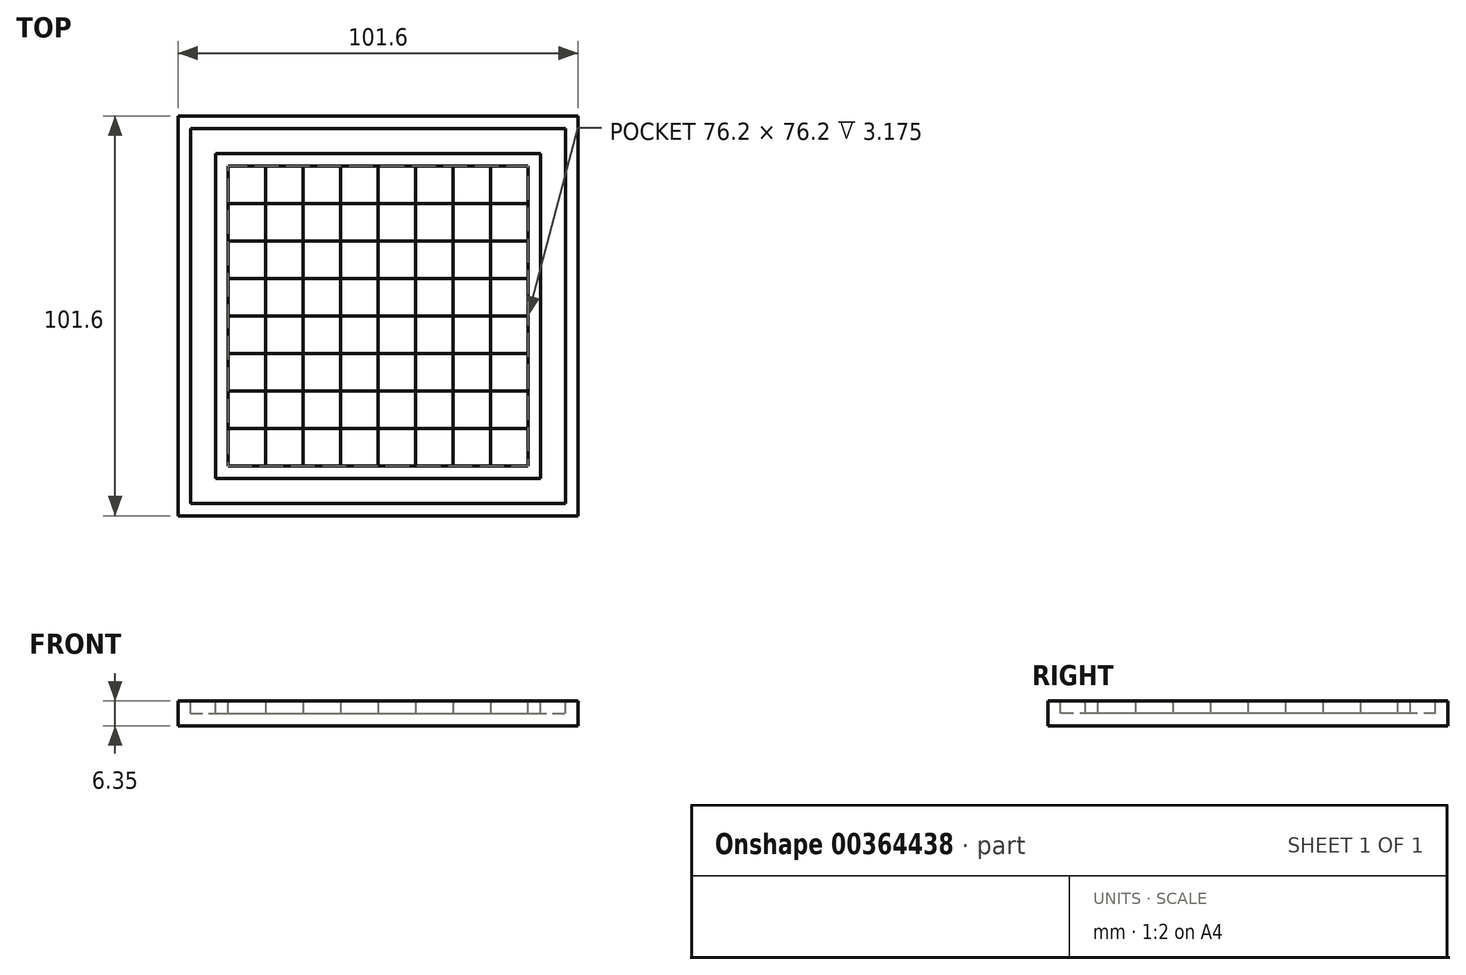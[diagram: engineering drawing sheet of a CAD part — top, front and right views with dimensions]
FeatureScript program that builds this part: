
annotation { "Feature Type Name" : "Feature", "Feature Type Description" : "" }
export const myFeature = defineFeature(function(context is Context, id is Id, definition is map)
    precondition{}
    {
        {
            var Q0;
            Q0=qCreatedBy(makeId("Top.planeOp"),FACE);
            var sketch = newSketch(context, id + "F0", { "sketchPlane" : qUnion([Q0])});
            skLineSegment(sketch, "E0.bottom", {"start": v(-50.8, 50.8) * mm, "end": v(50.8, 50.8) * mm});
            skLineSegment(sketch, "E0.top", {"start": v(-50.8, -50.8) * mm, "end": v(50.8, -50.8) * mm});
            skLineSegment(sketch, "E0.left", {"start": v(-50.8, 50.8) * mm, "end": v(-50.8, -50.8) * mm});
            skLineSegment(sketch, "E0.right", {"start": v(50.8, 50.8) * mm, "end": v(50.8, -50.8) * mm});
            skPoint(sketch, "E0.middle", {"position": v(0, 0) * mm});
            skSolve(sketch);
        }
        {
            var Q0;
            Q0 = qSketchRegion(id + "F0", true);
            extrude(context, id + "F1", {"entities" : qUnion([Q0]), "depth" : 6.35 * mm});
        }
        {
            var Q0;
            Q0=makeQuery(id+"F1.opExtrude","CAP_FACE",FACE,{"disambiguationData":[OSD([sQuery(id+"F0.wireOp",EDGE,"E0.bottom"),sQuery(id+"F0.wireOp",EDGE,"E0.top"),sQuery(id+"F0.wireOp",EDGE,"E0.left"),sQuery(id+"F0.wireOp",EDGE,"E0.right")])],"isStart":false});
            var sketch = newSketch(context, id + "F2", { "sketchPlane" : qUnion([Q0])});
            skLineSegment(sketch, "E1.bottom", {"start": v(-47.63, 47.63) * mm, "end": v(47.63, 47.63) * mm});
            skLineSegment(sketch, "E1.top", {"start": v(-47.63, -47.63) * mm, "end": v(47.63, -47.63) * mm});
            skLineSegment(sketch, "E1.left", {"start": v(-47.63, 47.63) * mm, "end": v(-47.63, -47.63) * mm});
            skLineSegment(sketch, "E1.right", {"start": v(47.63, 47.63) * mm, "end": v(47.63, -47.63) * mm});
            skPoint(sketch, "E1.middle", {"position": v(0, 0) * mm});
            skLineSegment(sketch, "E2.bottom", {"start": v(-41.28, 41.28) * mm, "end": v(41.28, 41.28) * mm});
            skLineSegment(sketch, "E2.top", {"start": v(-41.28, -41.27) * mm, "end": v(41.28, -41.27) * mm});
            skLineSegment(sketch, "E2.left", {"start": v(-41.28, 41.28) * mm, "end": v(-41.28, -41.28) * mm});
            skLineSegment(sketch, "E2.right", {"start": v(41.28, 41.28) * mm, "end": v(41.28, -41.28) * mm});
            skLineSegment(sketch, "E3.bottom", {"start": v(-38.1, 38.1) * mm, "end": v(38.1, 38.1) * mm});
            skLineSegment(sketch, "E3.top", {"start": v(-38.1, -38.1) * mm, "end": v(38.1, -38.1) * mm});
            skLineSegment(sketch, "E3.left", {"start": v(-38.1, 38.1) * mm, "end": v(-38.1, -38.1) * mm});
            skLineSegment(sketch, "E3.right", {"start": v(38.1, 38.1) * mm, "end": v(38.1, -38.1) * mm});
            skSolve(sketch);
        }
        {
            var Q0;
            Q0=makeQuery(id+"F2.imprint","IMPRINT",FACE,{"disambiguationData":[TD([[makeQuery(id+"F2.imprint","IMPRINT",EDGE,{"derivedFrom":sQuery(id+"F2.wireOp",EDGE,"E1.bottom")}),-1.0]])]});
            extrude(context, id + "F3", {"entities" : qUnion([Q0]), "operationType" : NewBodyOperationType.REMOVE, "oppositeDirection" : true, "depth" : 3.17 * mm});
        }
        {
            var Q0;
            Q0=makeQuery(id+"F2.imprint","IMPRINT",FACE,{"disambiguationData":[TD([[makeQuery(id+"F2.imprint","IMPRINT",EDGE,{"derivedFrom":sQuery(id+"F2.wireOp",EDGE,"E3.bottom")}),-1.0]])]});
            extrude(context, id + "F4", {"entities" : qUnion([Q0]), "operationType" : NewBodyOperationType.REMOVE, "oppositeDirection" : true, "depth" : 3.17 * mm});
        }
        {
            var Q0;
            Q0=makeQuery(id+"F4.boolean.opBoolean","COPY",FACE,{"derivedFrom":makeQuery(id+"F4.opExtrude","CAP_FACE",FACE,{"disambiguationData":[OSD([sQuery(id+"F2.wireOp",EDGE,"E3.bottom"),sQuery(id+"F2.wireOp",EDGE,"E3.top"),sQuery(id+"F2.wireOp",EDGE,"E3.left"),sQuery(id+"F2.wireOp",EDGE,"E3.right")])],"isStart":false})});
            var sketch = newSketch(context, id + "F5", { "sketchPlane" : qUnion([Q0])});
            skLineSegment(sketch, "E4", {"start": v(-28.58, 38.1) * mm, "end": v(-28.58, -38.1) * mm});
            skLineSegment(sketch, "E5", {"start": v(-19.05, 38.1) * mm, "end": v(-19.05, -38.1) * mm});
            skLineSegment(sketch, "E6", {"start": v(-9.53, 38.1) * mm, "end": v(-9.52, -38.1) * mm});
            skLineSegment(sketch, "E7", {"start": v(0, 38.1) * mm, "end": v(0, -38.1) * mm});
            skLineSegment(sketch, "E8", {"start": v(9.52, 38.1) * mm, "end": v(9.53, -38.1) * mm});
            skLineSegment(sketch, "E9", {"start": v(19.05, 38.1) * mm, "end": v(19.05, -38.1) * mm});
            skLineSegment(sketch, "E10", {"start": v(28.57, 38.1) * mm, "end": v(28.57, -38.1) * mm});
            skLineSegment(sketch, "E11", {"start": v(-38.1, 28.58) * mm, "end": v(38.1, 28.58) * mm});
            skLineSegment(sketch, "E12", {"start": v(-38.1, 19.05) * mm, "end": v(38.1, 19.05) * mm});
            skLineSegment(sketch, "E13", {"start": v(-38.1, 9.53) * mm, "end": v(38.1, 9.53) * mm});
            skLineSegment(sketch, "E14", {"start": v(-38.1, 0) * mm, "end": v(38.1, 0) * mm});
            skLineSegment(sketch, "E15", {"start": v(-38.1, -9.53) * mm, "end": v(38.1, -9.53) * mm});
            skLineSegment(sketch, "E16", {"start": v(-38.1, -19.05) * mm, "end": v(38.1, -19.05) * mm});
            skLineSegment(sketch, "E17", {"start": v(-38.1, -28.58) * mm, "end": v(38.1, -28.58) * mm});
            skSolve(sketch);
        }
        {
            var Q0;
            {var subQ0=sQuery(id+"F5.wireOp",EDGE,"E9");var subQ1=makeQuery(id+"F4.boolean.opBoolean","COPY",EDGE,{"derivedFrom":makeQuery(id+"F4.opExtrude","CAP_EDGE",EDGE,{"disambiguationData":[OSD([sQuery(id+"F2.wireOp",EDGE,"E3.top")])],"isStart":false})});var subQ2=makeQuery(id+"F5.imprint","INTERSECT",VERTEX,{"derivedFrom":[subQ1,subQ0]});Q0=makeQuery(id+"F5.imprint","IMPRINT",FACE,{"disambiguationData":[TD([[makeQuery(id+"F5.imprint","IMPRINT",EDGE,{"disambiguationData":[TD([[subQ2,1.0]])],"derivedFrom":subQ0}),1.0]])]});}
            var Q1;
            {var subQ0=sQuery(id+"F5.wireOp",EDGE,"E7");var subQ1=makeQuery(id+"F4.boolean.opBoolean","COPY",EDGE,{"derivedFrom":makeQuery(id+"F4.opExtrude","CAP_EDGE",EDGE,{"disambiguationData":[OSD([sQuery(id+"F2.wireOp",EDGE,"E3.top")])],"isStart":false})});var subQ2=makeQuery(id+"F5.imprint","INTERSECT",VERTEX,{"derivedFrom":[subQ1,subQ0]});Q1=makeQuery(id+"F5.imprint","IMPRINT",FACE,{"disambiguationData":[TD([[makeQuery(id+"F5.imprint","IMPRINT",EDGE,{"disambiguationData":[TD([[subQ2,1.0]])],"derivedFrom":subQ0}),1.0]])]});}
            var Q2;
            {var subQ0=sQuery(id+"F5.wireOp",EDGE,"E5");var subQ1=makeQuery(id+"F4.boolean.opBoolean","COPY",EDGE,{"derivedFrom":makeQuery(id+"F4.opExtrude","CAP_EDGE",EDGE,{"disambiguationData":[OSD([sQuery(id+"F2.wireOp",EDGE,"E3.top")])],"isStart":false})});var subQ2=makeQuery(id+"F5.imprint","INTERSECT",VERTEX,{"derivedFrom":[subQ1,subQ0]});Q2=makeQuery(id+"F5.imprint","IMPRINT",FACE,{"disambiguationData":[TD([[makeQuery(id+"F5.imprint","IMPRINT",EDGE,{"disambiguationData":[TD([[subQ2,1.0]])],"derivedFrom":subQ0}),1.0]])]});}
            var Q3;
            {var subQ0=sQuery(id+"F5.wireOp",EDGE,"E4");var subQ1=makeQuery(id+"F4.boolean.opBoolean","COPY",EDGE,{"derivedFrom":makeQuery(id+"F4.opExtrude","CAP_EDGE",EDGE,{"disambiguationData":[OSD([sQuery(id+"F2.wireOp",EDGE,"E3.top")])],"isStart":false})});var subQ2=makeQuery(id+"F5.imprint","INTERSECT",VERTEX,{"derivedFrom":[subQ1,subQ0]});Q3=makeQuery(id+"F5.imprint","IMPRINT",FACE,{"disambiguationData":[TD([[makeQuery(id+"F5.imprint","IMPRINT",EDGE,{"disambiguationData":[TD([[subQ2,1.0]])],"derivedFrom":subQ0}),-1.0]])]});}
            var Q4;
            {var subQ0=sQuery(id+"F5.wireOp",EDGE,"E16");var subQ1=sQuery(id+"F5.wireOp",EDGE,"E4");var subQ2=makeQuery(id+"F5.imprint","INTERSECT",VERTEX,{"derivedFrom":[subQ1,subQ0]});Q4=makeQuery(id+"F5.imprint","IMPRINT",FACE,{"disambiguationData":[TD([[makeQuery(id+"F5.imprint","IMPRINT",EDGE,{"disambiguationData":[TD([[subQ2,-1.0]])],"derivedFrom":subQ1}),1.0]])]});}
            var Q5;
            {var subQ0=sQuery(id+"F5.wireOp",EDGE,"E15");var subQ1=sQuery(id+"F5.wireOp",EDGE,"E4");var subQ2=makeQuery(id+"F5.imprint","INTERSECT",VERTEX,{"derivedFrom":[subQ1,subQ0]});Q5=makeQuery(id+"F5.imprint","IMPRINT",FACE,{"disambiguationData":[TD([[makeQuery(id+"F5.imprint","IMPRINT",EDGE,{"disambiguationData":[TD([[subQ2,-1.0]])],"derivedFrom":subQ1}),-1.0]])]});}
            var Q6;
            {var subQ0=sQuery(id+"F5.wireOp",EDGE,"E15");var subQ1=sQuery(id+"F5.wireOp",EDGE,"E5");var subQ2=makeQuery(id+"F5.imprint","INTERSECT",VERTEX,{"derivedFrom":[subQ1,subQ0]});Q6=makeQuery(id+"F5.imprint","IMPRINT",FACE,{"disambiguationData":[TD([[makeQuery(id+"F5.imprint","IMPRINT",EDGE,{"disambiguationData":[TD([[subQ2,-1.0]])],"derivedFrom":subQ1}),1.0]])]});}
            var Q7;
            {var subQ0=sQuery(id+"F5.wireOp",EDGE,"E14");var subQ1=sQuery(id+"F5.wireOp",EDGE,"E4");var subQ2=makeQuery(id+"F5.imprint","INTERSECT",VERTEX,{"derivedFrom":[subQ1,subQ0]});Q7=makeQuery(id+"F5.imprint","IMPRINT",FACE,{"disambiguationData":[TD([[makeQuery(id+"F5.imprint","IMPRINT",EDGE,{"disambiguationData":[TD([[subQ2,-1.0]])],"derivedFrom":subQ1}),1.0]])]});}
            var Q8;
            {var subQ0=sQuery(id+"F5.wireOp",EDGE,"E13");var subQ1=sQuery(id+"F5.wireOp",EDGE,"E4");var subQ2=makeQuery(id+"F5.imprint","INTERSECT",VERTEX,{"derivedFrom":[subQ1,subQ0]});Q8=makeQuery(id+"F5.imprint","IMPRINT",FACE,{"disambiguationData":[TD([[makeQuery(id+"F5.imprint","IMPRINT",EDGE,{"disambiguationData":[TD([[subQ2,-1.0]])],"derivedFrom":subQ1}),-1.0]])]});}
            var Q9;
            {var subQ0=sQuery(id+"F5.wireOp",EDGE,"E13");var subQ1=sQuery(id+"F5.wireOp",EDGE,"E5");var subQ2=makeQuery(id+"F5.imprint","INTERSECT",VERTEX,{"derivedFrom":[subQ1,subQ0]});Q9=makeQuery(id+"F5.imprint","IMPRINT",FACE,{"disambiguationData":[TD([[makeQuery(id+"F5.imprint","IMPRINT",EDGE,{"disambiguationData":[TD([[subQ2,-1.0]])],"derivedFrom":subQ1}),1.0]])]});}
            var Q10;
            {var subQ0=sQuery(id+"F5.wireOp",EDGE,"E12");var subQ1=sQuery(id+"F5.wireOp",EDGE,"E4");var subQ2=makeQuery(id+"F5.imprint","INTERSECT",VERTEX,{"derivedFrom":[subQ1,subQ0]});Q10=makeQuery(id+"F5.imprint","IMPRINT",FACE,{"disambiguationData":[TD([[makeQuery(id+"F5.imprint","IMPRINT",EDGE,{"disambiguationData":[TD([[subQ2,-1.0]])],"derivedFrom":subQ1}),1.0]])]});}
            var Q11;
            {var subQ0=sQuery(id+"F5.wireOp",EDGE,"E11");var subQ1=sQuery(id+"F5.wireOp",EDGE,"E4");var subQ2=makeQuery(id+"F5.imprint","INTERSECT",VERTEX,{"derivedFrom":[subQ1,subQ0]});Q11=makeQuery(id+"F5.imprint","IMPRINT",FACE,{"disambiguationData":[TD([[makeQuery(id+"F5.imprint","IMPRINT",EDGE,{"disambiguationData":[TD([[subQ2,-1.0]])],"derivedFrom":subQ1}),-1.0]])]});}
            var Q12;
            {var subQ0=sQuery(id+"F5.wireOp",EDGE,"E11");var subQ1=sQuery(id+"F5.wireOp",EDGE,"E5");var subQ2=makeQuery(id+"F5.imprint","INTERSECT",VERTEX,{"derivedFrom":[subQ1,subQ0]});Q12=makeQuery(id+"F5.imprint","IMPRINT",FACE,{"disambiguationData":[TD([[makeQuery(id+"F5.imprint","IMPRINT",EDGE,{"disambiguationData":[TD([[subQ2,-1.0]])],"derivedFrom":subQ1}),1.0]])]});}
            var Q13;
            {var subQ0=sQuery(id+"F5.wireOp",EDGE,"E4");var subQ1=makeQuery(id+"F4.boolean.opBoolean","COPY",EDGE,{"derivedFrom":makeQuery(id+"F4.opExtrude","CAP_EDGE",EDGE,{"disambiguationData":[OSD([sQuery(id+"F2.wireOp",EDGE,"E3.bottom")])],"isStart":false})});var subQ2=makeQuery(id+"F5.imprint","INTERSECT",VERTEX,{"derivedFrom":[subQ1,subQ0]});Q13=makeQuery(id+"F5.imprint","IMPRINT",FACE,{"disambiguationData":[TD([[makeQuery(id+"F5.imprint","IMPRINT",EDGE,{"disambiguationData":[TD([[subQ2,-1.0]])],"derivedFrom":subQ0}),1.0]])]});}
            var Q14;
            {var subQ0=sQuery(id+"F5.wireOp",EDGE,"E6");var subQ1=makeQuery(id+"F4.boolean.opBoolean","COPY",EDGE,{"derivedFrom":makeQuery(id+"F4.opExtrude","CAP_EDGE",EDGE,{"disambiguationData":[OSD([sQuery(id+"F2.wireOp",EDGE,"E3.bottom")])],"isStart":false})});var subQ2=makeQuery(id+"F5.imprint","INTERSECT",VERTEX,{"derivedFrom":[subQ1,subQ0]});Q14=makeQuery(id+"F5.imprint","IMPRINT",FACE,{"disambiguationData":[TD([[makeQuery(id+"F5.imprint","IMPRINT",EDGE,{"disambiguationData":[TD([[subQ2,-1.0]])],"derivedFrom":subQ0}),1.0]])]});}
            var Q15;
            {var subQ0=sQuery(id+"F5.wireOp",EDGE,"E11");var subQ1=sQuery(id+"F5.wireOp",EDGE,"E7");var subQ2=makeQuery(id+"F5.imprint","INTERSECT",VERTEX,{"derivedFrom":[subQ1,subQ0]});Q15=makeQuery(id+"F5.imprint","IMPRINT",FACE,{"disambiguationData":[TD([[makeQuery(id+"F5.imprint","IMPRINT",EDGE,{"disambiguationData":[TD([[subQ2,-1.0]])],"derivedFrom":subQ1}),1.0]])]});}
            var Q16;
            {var subQ0=sQuery(id+"F5.wireOp",EDGE,"E12");var subQ1=sQuery(id+"F5.wireOp",EDGE,"E6");var subQ2=makeQuery(id+"F5.imprint","INTERSECT",VERTEX,{"derivedFrom":[subQ1,subQ0]});Q16=makeQuery(id+"F5.imprint","IMPRINT",FACE,{"disambiguationData":[TD([[makeQuery(id+"F5.imprint","IMPRINT",EDGE,{"disambiguationData":[TD([[subQ2,-1.0]])],"derivedFrom":subQ1}),1.0]])]});}
            var Q17;
            {var subQ0=sQuery(id+"F5.wireOp",EDGE,"E13");var subQ1=sQuery(id+"F5.wireOp",EDGE,"E7");var subQ2=makeQuery(id+"F5.imprint","INTERSECT",VERTEX,{"derivedFrom":[subQ1,subQ0]});Q17=makeQuery(id+"F5.imprint","IMPRINT",FACE,{"disambiguationData":[TD([[makeQuery(id+"F5.imprint","IMPRINT",EDGE,{"disambiguationData":[TD([[subQ2,-1.0]])],"derivedFrom":subQ1}),1.0]])]});}
            var Q18;
            {var subQ0=sQuery(id+"F5.wireOp",EDGE,"E14");var subQ1=sQuery(id+"F5.wireOp",EDGE,"E6");var subQ2=makeQuery(id+"F5.imprint","INTERSECT",VERTEX,{"derivedFrom":[subQ1,subQ0]});Q18=makeQuery(id+"F5.imprint","IMPRINT",FACE,{"disambiguationData":[TD([[makeQuery(id+"F5.imprint","IMPRINT",EDGE,{"disambiguationData":[TD([[subQ2,-1.0]])],"derivedFrom":subQ1}),1.0]])]});}
            var Q19;
            {var subQ0=sQuery(id+"F5.wireOp",EDGE,"E15");var subQ1=sQuery(id+"F5.wireOp",EDGE,"E7");var subQ2=makeQuery(id+"F5.imprint","INTERSECT",VERTEX,{"derivedFrom":[subQ1,subQ0]});Q19=makeQuery(id+"F5.imprint","IMPRINT",FACE,{"disambiguationData":[TD([[makeQuery(id+"F5.imprint","IMPRINT",EDGE,{"disambiguationData":[TD([[subQ2,-1.0]])],"derivedFrom":subQ1}),1.0]])]});}
            var Q20;
            {var subQ0=sQuery(id+"F5.wireOp",EDGE,"E16");var subQ1=sQuery(id+"F5.wireOp",EDGE,"E6");var subQ2=makeQuery(id+"F5.imprint","INTERSECT",VERTEX,{"derivedFrom":[subQ1,subQ0]});Q20=makeQuery(id+"F5.imprint","IMPRINT",FACE,{"disambiguationData":[TD([[makeQuery(id+"F5.imprint","IMPRINT",EDGE,{"disambiguationData":[TD([[subQ2,-1.0]])],"derivedFrom":subQ1}),1.0]])]});}
            var Q21;
            {var subQ0=sQuery(id+"F5.wireOp",EDGE,"E16");var subQ1=sQuery(id+"F5.wireOp",EDGE,"E8");var subQ2=makeQuery(id+"F5.imprint","INTERSECT",VERTEX,{"derivedFrom":[subQ1,subQ0]});Q21=makeQuery(id+"F5.imprint","IMPRINT",FACE,{"disambiguationData":[TD([[makeQuery(id+"F5.imprint","IMPRINT",EDGE,{"disambiguationData":[TD([[subQ2,-1.0]])],"derivedFrom":subQ1}),1.0]])]});}
            var Q22;
            {var subQ0=sQuery(id+"F5.wireOp",EDGE,"E15");var subQ1=sQuery(id+"F5.wireOp",EDGE,"E9");var subQ2=makeQuery(id+"F5.imprint","INTERSECT",VERTEX,{"derivedFrom":[subQ1,subQ0]});Q22=makeQuery(id+"F5.imprint","IMPRINT",FACE,{"disambiguationData":[TD([[makeQuery(id+"F5.imprint","IMPRINT",EDGE,{"disambiguationData":[TD([[subQ2,-1.0]])],"derivedFrom":subQ1}),1.0]])]});}
            var Q23;
            {var subQ0=sQuery(id+"F5.wireOp",EDGE,"E14");var subQ1=sQuery(id+"F5.wireOp",EDGE,"E8");var subQ2=makeQuery(id+"F5.imprint","INTERSECT",VERTEX,{"derivedFrom":[subQ1,subQ0]});Q23=makeQuery(id+"F5.imprint","IMPRINT",FACE,{"disambiguationData":[TD([[makeQuery(id+"F5.imprint","IMPRINT",EDGE,{"disambiguationData":[TD([[subQ2,-1.0]])],"derivedFrom":subQ1}),1.0]])]});}
            var Q24;
            {var subQ0=sQuery(id+"F5.wireOp",EDGE,"E13");var subQ1=sQuery(id+"F5.wireOp",EDGE,"E9");var subQ2=makeQuery(id+"F5.imprint","INTERSECT",VERTEX,{"derivedFrom":[subQ1,subQ0]});Q24=makeQuery(id+"F5.imprint","IMPRINT",FACE,{"disambiguationData":[TD([[makeQuery(id+"F5.imprint","IMPRINT",EDGE,{"disambiguationData":[TD([[subQ2,-1.0]])],"derivedFrom":subQ1}),1.0]])]});}
            var Q25;
            {var subQ0=sQuery(id+"F5.wireOp",EDGE,"E12");var subQ1=sQuery(id+"F5.wireOp",EDGE,"E8");var subQ2=makeQuery(id+"F5.imprint","INTERSECT",VERTEX,{"derivedFrom":[subQ1,subQ0]});Q25=makeQuery(id+"F5.imprint","IMPRINT",FACE,{"disambiguationData":[TD([[makeQuery(id+"F5.imprint","IMPRINT",EDGE,{"disambiguationData":[TD([[subQ2,-1.0]])],"derivedFrom":subQ1}),1.0]])]});}
            var Q26;
            {var subQ0=sQuery(id+"F5.wireOp",EDGE,"E11");var subQ1=sQuery(id+"F5.wireOp",EDGE,"E9");var subQ2=makeQuery(id+"F5.imprint","INTERSECT",VERTEX,{"derivedFrom":[subQ1,subQ0]});Q26=makeQuery(id+"F5.imprint","IMPRINT",FACE,{"disambiguationData":[TD([[makeQuery(id+"F5.imprint","IMPRINT",EDGE,{"disambiguationData":[TD([[subQ2,-1.0]])],"derivedFrom":subQ1}),1.0]])]});}
            var Q27;
            {var subQ0=sQuery(id+"F5.wireOp",EDGE,"E8");var subQ1=makeQuery(id+"F4.boolean.opBoolean","COPY",EDGE,{"derivedFrom":makeQuery(id+"F4.opExtrude","CAP_EDGE",EDGE,{"disambiguationData":[OSD([sQuery(id+"F2.wireOp",EDGE,"E3.bottom")])],"isStart":false})});var subQ2=makeQuery(id+"F5.imprint","INTERSECT",VERTEX,{"derivedFrom":[subQ1,subQ0]});Q27=makeQuery(id+"F5.imprint","IMPRINT",FACE,{"disambiguationData":[TD([[makeQuery(id+"F5.imprint","IMPRINT",EDGE,{"disambiguationData":[TD([[subQ2,-1.0]])],"derivedFrom":subQ0}),1.0]])]});}
            var Q28;
            {var subQ0=sQuery(id+"F5.wireOp",EDGE,"E10");var subQ1=makeQuery(id+"F4.boolean.opBoolean","COPY",EDGE,{"derivedFrom":makeQuery(id+"F4.opExtrude","CAP_EDGE",EDGE,{"disambiguationData":[OSD([sQuery(id+"F2.wireOp",EDGE,"E3.bottom")])],"isStart":false})});var subQ2=makeQuery(id+"F5.imprint","INTERSECT",VERTEX,{"derivedFrom":[subQ1,subQ0]});Q28=makeQuery(id+"F5.imprint","IMPRINT",FACE,{"disambiguationData":[TD([[makeQuery(id+"F5.imprint","IMPRINT",EDGE,{"disambiguationData":[TD([[subQ2,-1.0]])],"derivedFrom":subQ0}),1.0]])]});}
            var Q29;
            {var subQ0=sQuery(id+"F5.wireOp",EDGE,"E12");var subQ1=sQuery(id+"F5.wireOp",EDGE,"E10");var subQ2=makeQuery(id+"F5.imprint","INTERSECT",VERTEX,{"derivedFrom":[subQ1,subQ0]});Q29=makeQuery(id+"F5.imprint","IMPRINT",FACE,{"disambiguationData":[TD([[makeQuery(id+"F5.imprint","IMPRINT",EDGE,{"disambiguationData":[TD([[subQ2,-1.0]])],"derivedFrom":subQ1}),1.0]])]});}
            var Q30;
            {var subQ0=sQuery(id+"F5.wireOp",EDGE,"E14");var subQ1=sQuery(id+"F5.wireOp",EDGE,"E10");var subQ2=makeQuery(id+"F5.imprint","INTERSECT",VERTEX,{"derivedFrom":[subQ1,subQ0]});Q30=makeQuery(id+"F5.imprint","IMPRINT",FACE,{"disambiguationData":[TD([[makeQuery(id+"F5.imprint","IMPRINT",EDGE,{"disambiguationData":[TD([[subQ2,-1.0]])],"derivedFrom":subQ1}),1.0]])]});}
            var Q31;
            {var subQ0=sQuery(id+"F5.wireOp",EDGE,"E16");var subQ1=sQuery(id+"F5.wireOp",EDGE,"E10");var subQ2=makeQuery(id+"F5.imprint","INTERSECT",VERTEX,{"derivedFrom":[subQ1,subQ0]});Q31=makeQuery(id+"F5.imprint","IMPRINT",FACE,{"disambiguationData":[TD([[makeQuery(id+"F5.imprint","IMPRINT",EDGE,{"disambiguationData":[TD([[subQ2,-1.0]])],"derivedFrom":subQ1}),1.0]])]});}
            extrude(context, id + "F6", {"entities" : qUnion([Q0, Q1, Q2, Q3, Q4, Q5, Q6, Q7, Q8, Q9, Q10, Q11, Q12, Q13, Q14, Q15, Q16, Q17, Q18, Q19, Q20, Q21, Q22, Q23, Q24, Q25, Q26, Q27, Q28, Q29, Q30, Q31]), "depth" : 3.17 * mm});
        }
    });
